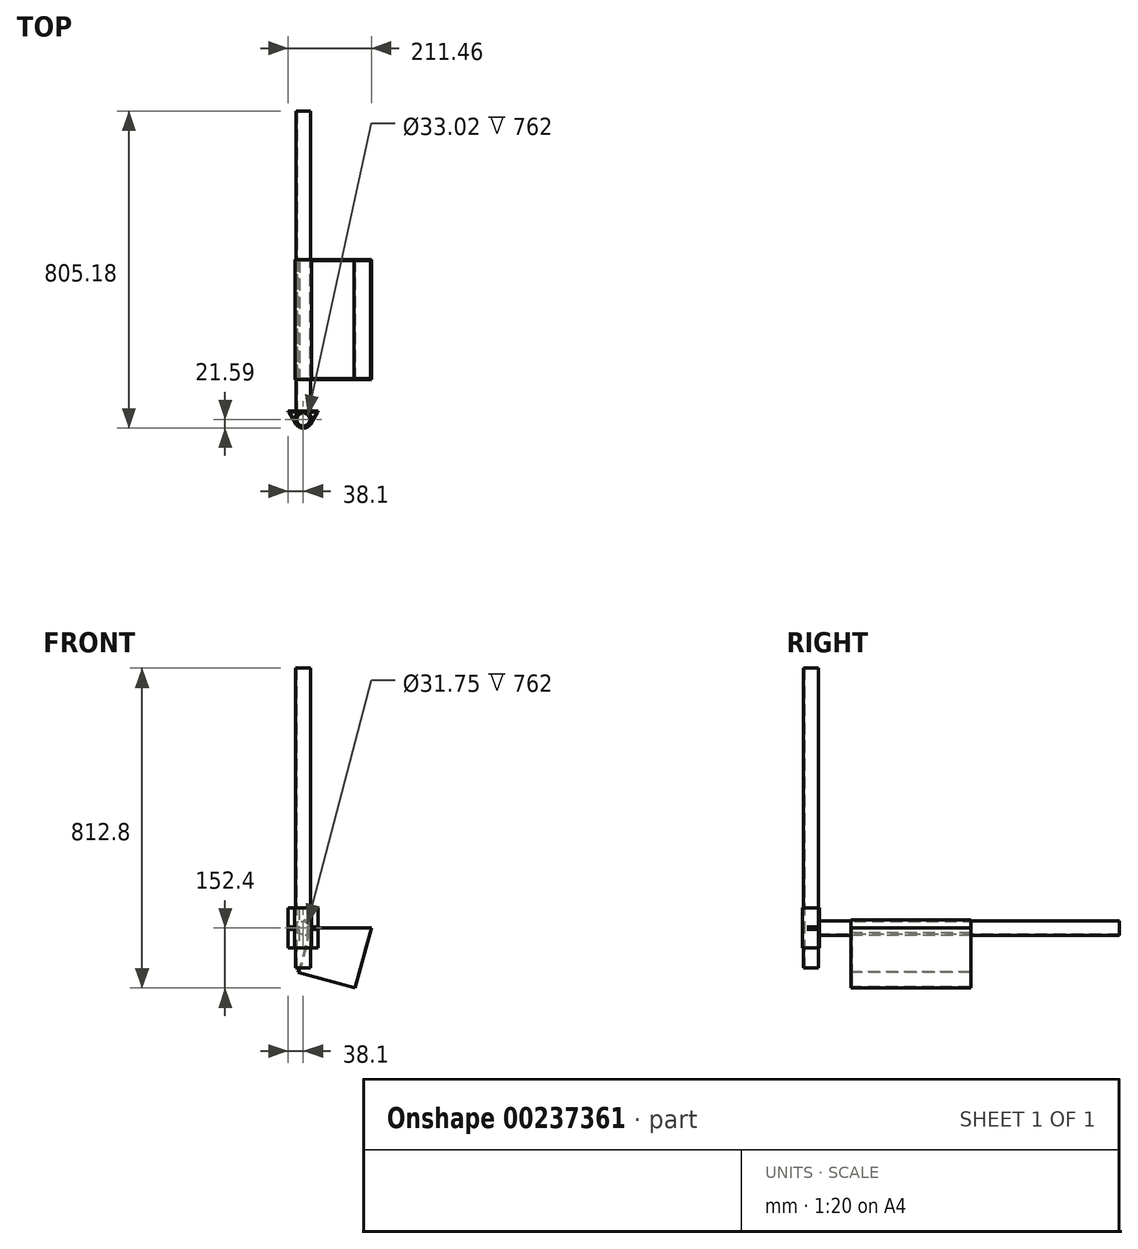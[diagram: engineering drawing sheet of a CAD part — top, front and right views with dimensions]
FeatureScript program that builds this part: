
annotation { "Feature Type Name" : "Feature", "Feature Type Description" : "" }
export const myFeature = defineFeature(function(context is Context, id is Id, definition is map)
    precondition{}
    {
        {
            var Q0;
            Q0=qCreatedBy(makeId("Top.planeOp"),FACE);
            var sketch = newSketch(context, id + "F0", { "sketchPlane" : qUnion([Q0])});
            skCircle(sketch, "E0", {"center": v(0, 0) * mm, "radius": 19.05 * mm});
            skCircle(sketch, "E1", {"center": v(0, 0) * mm, "radius": 16.51 * mm});
            skSolve(sketch);
        }
        {
            var Q0;
            Q0 = qSketchRegion(id + "F0", true);
            extrude(context, id + "F1", {"entities" : qUnion([Q0]), "depth" : 762 * mm});
        }
        {
            var Q0;
            Q0=qCreatedBy(makeId("Top.planeOp"),FACE);
            cPlane(context, id + "F2", {"entities" : qUnion([Q0]), "cplaneType" : CPlaneType.OFFSET, "offset" : 101.6 * mm, "width" : 152.4 * mm, "height" : 152.4 * mm});
        }
        {
            var Q0;
            Q0=qCreatedBy(id+"F2.planeOp",FACE);
            var sketch = newSketch(context, id + "F3", { "sketchPlane" : qUnion([Q0])});
            skCircle(sketch, "E2.0", {"center": v(0, 0) * mm, "radius": 19.05 * mm});
            skCircle(sketch, "E3.0", {"center": v(0, 0) * mm, "radius": 21.59 * mm});
            skLineSegment(sketch, "E4", {"start": v(-18.52, -11.1) * mm, "end": v(-38.1, 21.6) * mm});
            skLineSegment(sketch, "E5", {"start": v(18.52, -11.1) * mm, "end": v(38.1, 21.6) * mm});
            skLineSegment(sketch, "E6", {"start": v(-38.1, 21.59) * mm, "end": v(38.1, 21.6) * mm});
            skLineSegment(sketch, "E7", {"start": v(0, 0) * mm, "end": v(0, 52.3) * mm, "construction": true});
            skSolve(sketch);
        }
        {
            var Q0;
            Q0=makeQuery(id+"F3.imprint","IMPRINT",FACE,{"disambiguationData":[TD([[makeQuery(id+"F3.imprint","IMPRINT",EDGE,{"derivedFrom":sQuery(id+"F3.wireOp",EDGE,"E2.0")}),-1.0]])]});
            extrude(context, id + "F4", {"entities" : qUnion([Q0]), "endBound" : BoundingType.SYMMETRIC, "depth" : 101.6 * mm});
        }
        {
            var Q0;
            {var subQ0=sQuery(id+"F3.wireOp",EDGE,"E5");Q0=makeQuery(id+"F3.imprint","IMPRINT",FACE,{"disambiguationData":[TD([[makeQuery(id+"F3.imprint","IMPRINT",EDGE,{"derivedFrom":subQ0}),1.0]])]});}
            var Q1;
            {var subQ0=sQuery(id+"F3.wireOp",EDGE,"E4");Q1=makeQuery(id+"F3.imprint","IMPRINT",FACE,{"disambiguationData":[TD([[makeQuery(id+"F3.imprint","IMPRINT",EDGE,{"derivedFrom":subQ0}),-1.0]])]});}
            extrude(context, id + "F5", {"entities" : qUnion([Q0, Q1]), "operationType" : NewBodyOperationType.ADD, "endBound" : BoundingType.SYMMETRIC, "depth" : 6.35 * mm});
        }
        {
            var Q0;
            {var subQ0=sQuery(id+"F3.wireOp",EDGE,"E6");Q0=makeQuery(id+"F5.boolean.opBoolean","MERGE",FACE,{"derivedFrom":[makeQuery(id+"F5.opExtrude","SWEPT_FACE",FACE,{"disambiguationData":[OSD([subQ0]),TDD([makeQuery(id+"F3.imprint","IMPRINT",EDGE,{"disambiguationData":[TD([[makeQuery(id+"F3.imprint","INTERSECT",VERTEX,{"derivedFrom":[sQuery(id+"F3.wireOp",EDGE,"E4"),subQ0]}),-1.0]])],"derivedFrom":subQ0})])]}),makeQuery(id+"F5.opExtrude","SWEPT_FACE",FACE,{"disambiguationData":[OSD([subQ0]),TDD([makeQuery(id+"F3.imprint","IMPRINT",EDGE,{"disambiguationData":[TD([[makeQuery(id+"F3.imprint","INTERSECT",VERTEX,{"derivedFrom":[sQuery(id+"F3.wireOp",EDGE,"E5"),subQ0]}),1.0]])],"derivedFrom":subQ0})])]})]});}
            var sketch = newSketch(context, id + "F6", { "sketchPlane" : qUnion([Q0])});
            skLineSegment(sketch, "E8.0", {"start": v(38.1, 101.6) * mm, "end": v(-38.1, 101.6) * mm, "construction": true});
            skLineSegment(sketch, "E9.bottom", {"start": v(38.1, 152.4) * mm, "end": v(-38.1, 152.4) * mm});
            skLineSegment(sketch, "E9.top", {"start": v(38.1, 50.8) * mm, "end": v(-38.1, 50.8) * mm});
            skLineSegment(sketch, "E9.left", {"start": v(38.1, 152.4) * mm, "end": v(38.1, 50.8) * mm});
            skLineSegment(sketch, "E9.right", {"start": v(-38.1, 152.4) * mm, "end": v(-38.1, 50.8) * mm});
            skPoint(sketch, "E9.middle", {"position": v(0, 101.6) * mm});
            skSolve(sketch);
        }
        {
            var Q0;
            {var subQ4=sQuery(id+"F6.wireOp",EDGE,"E9.bottom");Q0=makeQuery(id+"F6.imprint","IMPRINT",FACE,{"disambiguationData":[TD([[makeQuery(id+"F6.imprint","IMPRINT",EDGE,{"derivedFrom":subQ4}),1.0]])]});}
            var Q1;
            {var subQ3=sQuery(id+"F6.wireOp",EDGE,"E9.top");Q1=makeQuery(id+"F6.imprint","IMPRINT",FACE,{"disambiguationData":[TD([[makeQuery(id+"F6.imprint","IMPRINT",EDGE,{"derivedFrom":subQ3}),-1.0]])]});}
            var Q2;
            {var subQ0=sQuery(id+"F3.wireOp",EDGE,"E6");var subQ2=makeQuery(id+"F3.imprint","IMPRINT",EDGE,{"disambiguationData":[TD([[makeQuery(id+"F3.imprint","INTERSECT",VERTEX,{"derivedFrom":[sQuery(id+"F3.wireOp",EDGE,"E4"),subQ0]}),-1.0]])],"derivedFrom":subQ0});var subQ4=makeQuery(id+"F5.opExtrude","CAP_EDGE",EDGE,{"disambiguationData":[OSD([subQ0]),TDD([subQ2])],"isStart":true});Q2=makeQuery(id+"F6.imprint","IMPRINT",FACE,{"disambiguationData":[TD([[makeQuery(id+"F6.imprint","IMPRINT",EDGE,{"derivedFrom":subQ4}),-1.0]])]});}
            extrude(context, id + "F7", {"entities" : qUnion([Q0, Q1, Q2]), "operationType" : NewBodyOperationType.ADD, "oppositeDirection" : true, "depth" : 2.54 * mm});
        }
        {
            var Q0;
            {var subQ0=sQuery(id+"F3.wireOp",EDGE,"E6");Q0=makeQuery(id+"F7.boolean.opBoolean","MERGE",FACE,{"derivedFrom":[makeQuery(id+"F5.boolean.opBoolean","MERGE",FACE,{"derivedFrom":[makeQuery(id+"F5.opExtrude","SWEPT_FACE",FACE,{"disambiguationData":[OSD([subQ0]),TDD([makeQuery(id+"F3.imprint","IMPRINT",EDGE,{"disambiguationData":[TD([[makeQuery(id+"F3.imprint","INTERSECT",VERTEX,{"derivedFrom":[sQuery(id+"F3.wireOp",EDGE,"E4"),subQ0]}),-1.0]])],"derivedFrom":subQ0})])]}),makeQuery(id+"F5.opExtrude","SWEPT_FACE",FACE,{"disambiguationData":[OSD([subQ0]),TDD([makeQuery(id+"F3.imprint","IMPRINT",EDGE,{"disambiguationData":[TD([[makeQuery(id+"F3.imprint","INTERSECT",VERTEX,{"derivedFrom":[sQuery(id+"F3.wireOp",EDGE,"E5"),subQ0]}),1.0]])],"derivedFrom":subQ0})])]})]}),makeQuery(id+"F7.opExtrude","CAP_FACE",FACE,{"disambiguationData":[OSD([sQuery(id+"F6.wireOp",EDGE,"E9.bottom"),sQuery(id+"F6.wireOp",EDGE,"E9.top"),sQuery(id+"F6.wireOp",EDGE,"E9.left"),sQuery(id+"F6.wireOp",EDGE,"E9.right")])],"isStart":true})]});}
            var sketch = newSketch(context, id + "F8", { "sketchPlane" : qUnion([Q0])});
            skLineSegment(sketch, "E10", {"start": v(0, 50.8) * mm, "end": v(0, 152.4) * mm, "construction": true});
            skCircle(sketch, "E11", {"center": v(0, 101.6) * mm, "radius": 15.88 * mm});
            skCircle(sketch, "E12", {"center": v(0, 101.6) * mm, "radius": 18.41 * mm});
            skSolve(sketch);
        }
        {
            var Q0;
            Q0 = qSketchRegion(id + "F8", true);
            extrude(context, id + "F9", {"entities" : qUnion([Q0]), "operationType" : NewBodyOperationType.ADD, "depth" : 762 * mm});
        }
        {
            var Q0;
            Q0=qCreatedBy(makeId("Front.planeOp"),FACE);
            cPlane(context, id + "F10", {"entities" : qUnion([Q0]), "cplaneType" : CPlaneType.OFFSET, "offset" : 101.6 * mm, "oppositeDirection" : true, "width" : 152.4 * mm, "height" : 152.4 * mm});
        }
        {
            var Q0;
            Q0=qCreatedBy(id+"F10.planeOp",FACE);
            var sketch = newSketch(context, id + "F11", { "sketchPlane" : qUnion([Q0])});
            skArc(sketch, "E13.0", {"start": v(18.41, 101.6) * mm, "mid": v(0, 120.02) * mm, "end": v(-18.42, 101.6) * mm});
            skArc(sketch, "E14.0", {"start": v(20.95, 101.6) * mm, "mid": v(0, 122.56) * mm, "end": v(-20.96, 101.6) * mm});
            skLineSegment(sketch, "E15", {"start": v(173.35, 101.6) * mm, "end": v(131.25, -50.8) * mm});
            skLineSegment(sketch, "E16", {"start": v(-12.7, -11.03) * mm, "end": v(131.25, -50.8) * mm});
            skLineSegment(sketch, "E17", {"start": v(20.95, 101.6) * mm, "end": v(173.35, 101.6) * mm});
            skLineSegment(sketch, "E18", {"start": v(18.41, 101.6) * mm, "end": v(-12.7, -11.03) * mm});
            skLineSegment(sketch, "E19", {"start": v(-18.41, 101.6) * mm, "end": v(-20.95, 101.6) * mm, "construction": true});
            skLineSegment(sketch, "E20", {"start": v(-20.96, 101.6) * mm, "end": v(-20.96, 88.9) * mm});
            skLineSegment(sketch, "E21", {"start": v(-20.96, 88.9) * mm, "end": v(-18.41, 88.9) * mm});
            skLineSegment(sketch, "E22", {"start": v(-18.41, 88.9) * mm, "end": v(-18.41, 101.6) * mm});
            skSolve(sketch);
        }
        {
            var Q0;
            Q0 = qSketchRegion(id + "F11", true);
            extrude(context, id + "F12", {"entities" : qUnion([Q0]), "oppositeDirection" : true, "depth" : 304.8 * mm});
        }
        {
            var Q0;
            Q0=makeQuery(id+"F12.opExtrude","SWEPT_FACE",FACE,{"disambiguationData":[OSD([sQuery(id+"F11.wireOp",EDGE,"E17")])]});
            shell(context, id + "F13", {"entities" : qUnion([Q0]), "thickness" : 2.54 * mm});
        }
    });
